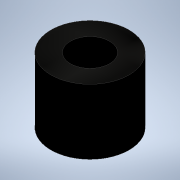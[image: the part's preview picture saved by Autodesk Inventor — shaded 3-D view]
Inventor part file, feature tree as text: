
AUTODESK INVENTOR PART (.ipt)
format: ipt  version: 2020.2 (Build 242310000, 310)  size: 90,624 bytes
history: native  units: mm
features: other x1, extrude x1, sketch x1
ambient origin geometry x8: Origin, YZ Plane, XZ Plane, XY Plane, X Axis, Y Axis, Z Axis, Center Point
bodies: Body1 (feature_tree)
feature tree (3):
  other  "ソリッド1"
  extrude  "押し出し1"  Depth=6.0mm
  sketch  "スケッチ1"
